# Revit family: Arcos-P-I
name_source: partatom
category: Lighting Fixtures
revit_build: Autodesk Revit 2014 (Build: 20130308_1515(x64)
units: mm (PartAtom-declared; Revit-internal decimal feet)

## types (2) — shared parameters
Apparent Load = 0 VA
Assembly Code = D5020210
Color Filter = 16777215
Default Elevation = 4' - 0"
Description = Arcos Perf is an indirect fixture with a classic curve  clean, simple, efficient. A superior optical system with T5, T5HO, and T8 lamping options provides flexibility for a wide variety of architectural space requirements.
Dimming Lamp Color Temperature Shift = <None>
Emit Shape Visible in Rendering = No
Emit from Rectangle Length = 0' - 4"
Fixture Distribution = Indirect
Glass = Glass - Hubbell - Perforated
Housing Material = Paint - Hubbell - Matte White
Lamp = Fluorescent
Load Classification = Lighting
Manufacturer = Litecontrol Lighting
Model = Arcos Pendant Indirect
Mounting = Pendant
Photometric Link = https://www.hubbell.com
Photometric Notes = More IES files download on Photometric Link
Photometric Web File = 59-P-I-04-SGL-Cx-1T5HO.ies
Power Factor = 1
Product Documentation Link = https://hubbellcdn.com
Product Page URL = https://www.hubbell.com
Tilt Angle = -90.00°
Type Comments = Lighting Fixture
URL = https://www.hubbell.com
Voltage = 120 V
Warranty = 5-Years Warranty

## per-type parameters (varying)
| type | Emit from Rectangle Width | zz Length 1 |
| Arcos-P-I-04 | 3' - 10" | 4' - 0" |
| Arcos-P-I-08 | 7' - 10" | 8' - 0" |

## geometry (parser evidence)
native form markers: Sweep x4
no freeform markers — native parametric forms only
